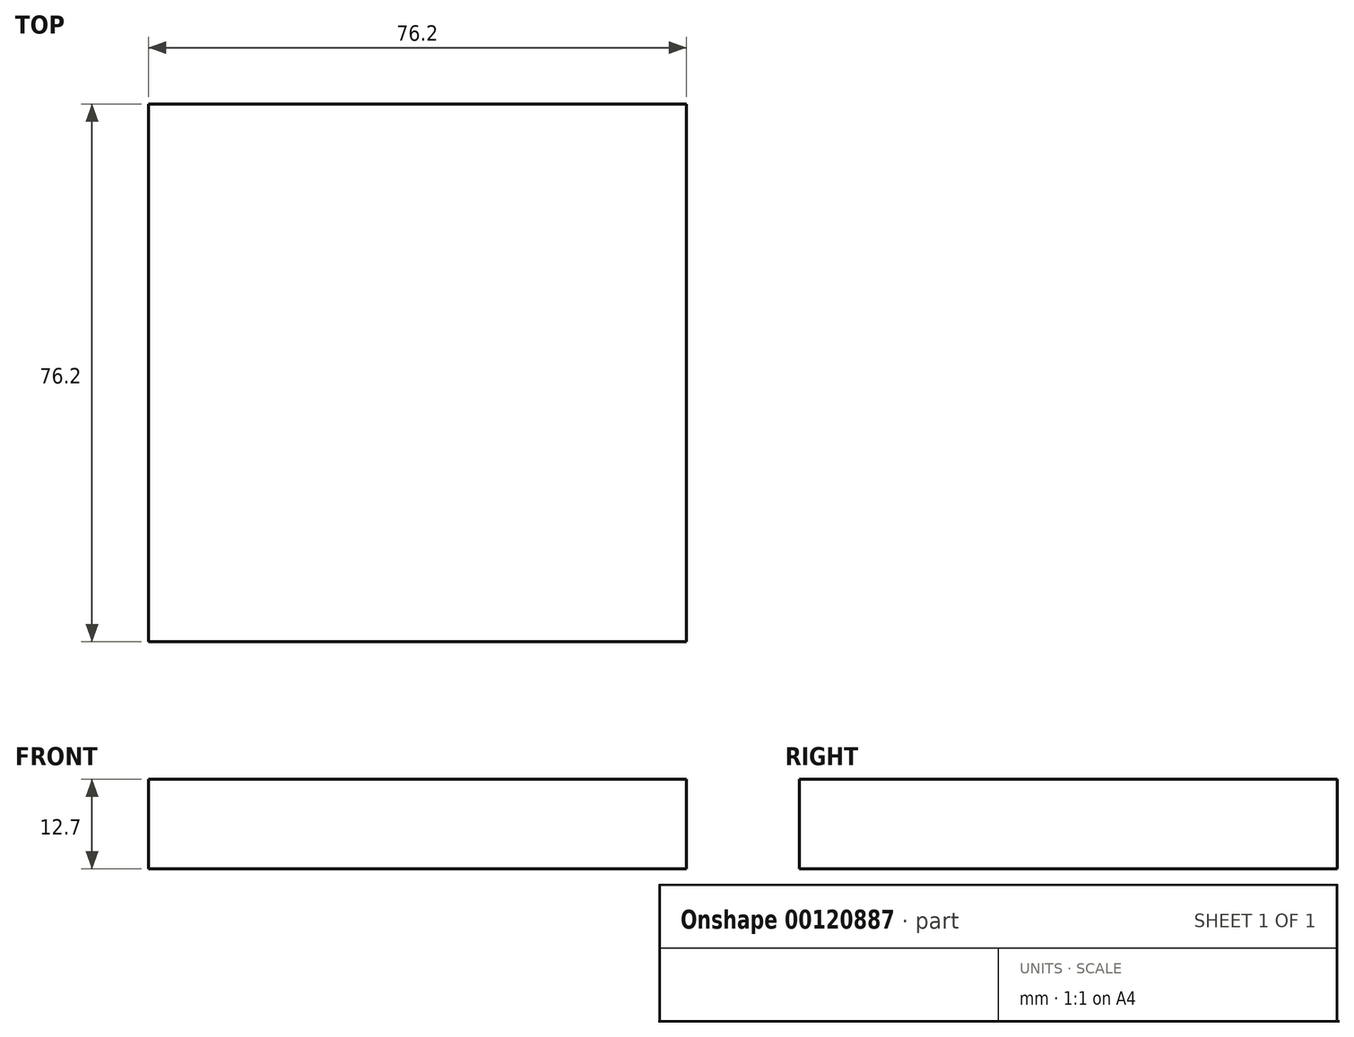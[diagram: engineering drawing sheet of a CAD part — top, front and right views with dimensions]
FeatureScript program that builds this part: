
annotation { "Feature Type Name" : "Feature", "Feature Type Description" : "" }
export const myFeature = defineFeature(function(context is Context, id is Id, definition is map)
    precondition{}
    {
        {
            var Q0;
            Q0=qCreatedBy(makeId("Top.planeOp"),FACE);
            var sketch = newSketch(context, id + "F0", { "sketchPlane" : qUnion([Q0])});
            skLineSegment(sketch, "E0.bottom", {"start": v(-35.68, 38.75) * mm, "end": v(40.52, 38.75) * mm});
            skLineSegment(sketch, "E0.top", {"start": v(-35.68, -37.45) * mm, "end": v(40.52, -37.45) * mm});
            skLineSegment(sketch, "E0.left", {"start": v(-35.68, 38.75) * mm, "end": v(-35.68, -37.45) * mm});
            skLineSegment(sketch, "E0.right", {"start": v(40.52, 38.75) * mm, "end": v(40.52, -37.45) * mm});
            skSolve(sketch);
        }
        {
            var Q0;
            Q0=makeQuery(id+"F0.imprint","IMPRINT",FACE,{"disambiguationData":[TD([[makeQuery(id+"F0.imprint","IMPRINT",EDGE,{"derivedFrom":sQuery(id+"F0.wireOp",EDGE,"E0.bottom")}),-1.0]])]});
            extrude(context, id + "F1", {"entities" : qUnion([Q0]), "depth" : 12.7 * mm});
        }
    });
